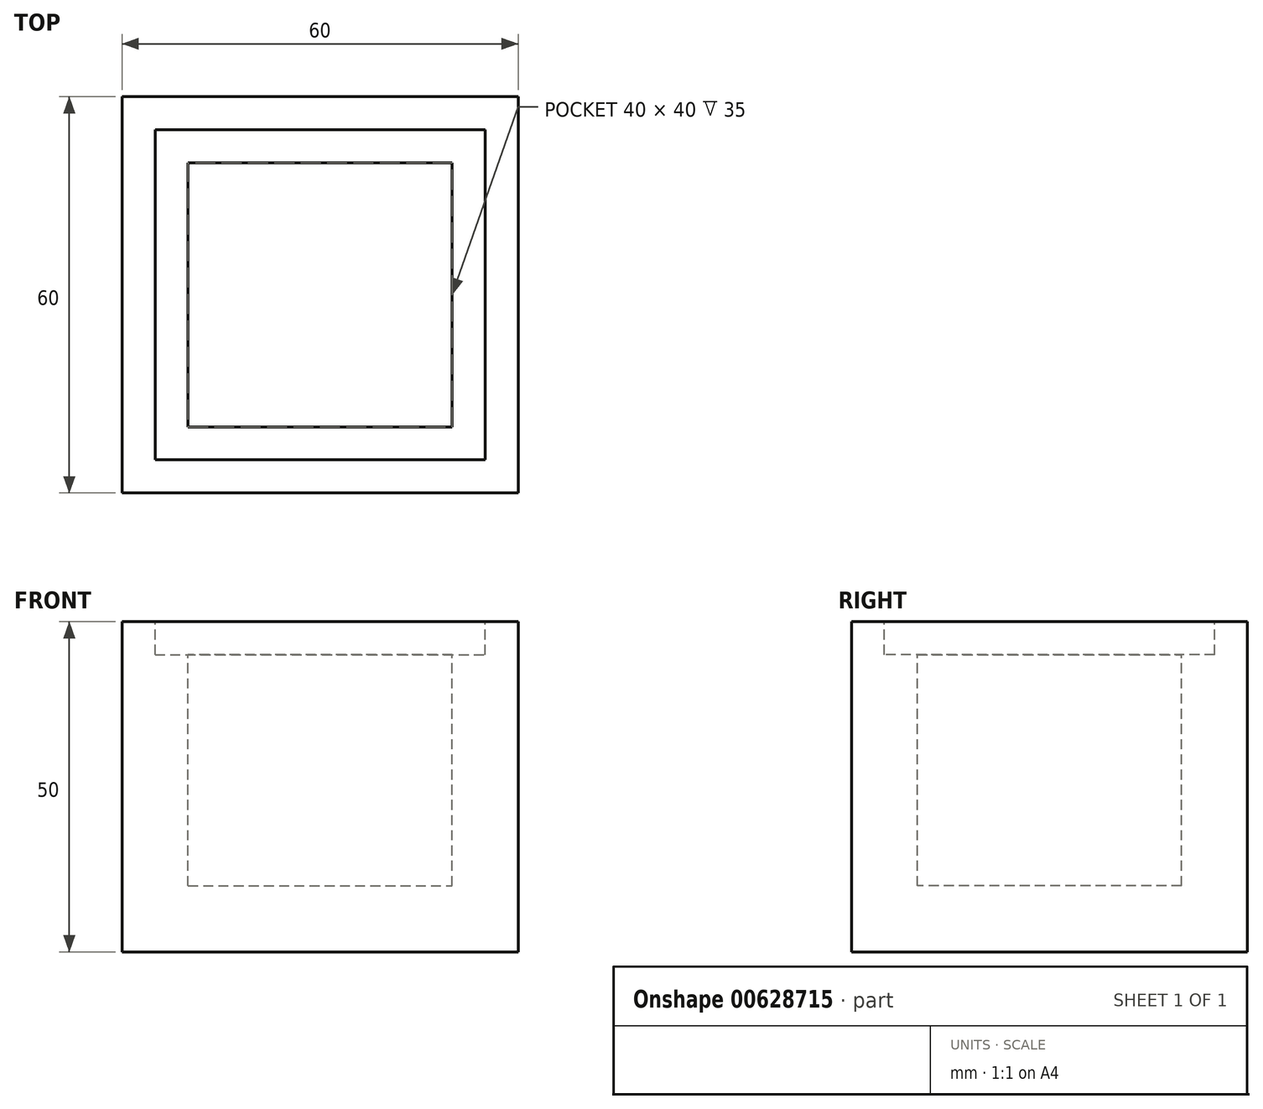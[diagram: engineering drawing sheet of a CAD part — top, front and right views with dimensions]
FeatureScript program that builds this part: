
annotation { "Feature Type Name" : "Feature", "Feature Type Description" : "" }
export const myFeature = defineFeature(function(context is Context, id is Id, definition is map)
    precondition{}
    {
        {
            var Q0;
            Q0=qCreatedBy(makeId("Top.planeOp"),FACE);
            var sketch = newSketch(context, id + "F0", { "sketchPlane" : qUnion([Q0])});
            skLineSegment(sketch, "E0.bottom", {"start": v(0, 0) * mm, "end": v(60, 0) * mm});
            skLineSegment(sketch, "E0.top", {"start": v(0, 60) * mm, "end": v(60, 60) * mm});
            skLineSegment(sketch, "E0.left", {"start": v(0, 0) * mm, "end": v(0, 60) * mm});
            skLineSegment(sketch, "E0.right", {"start": v(60, 0) * mm, "end": v(60, 60) * mm});
            skSolve(sketch);
        }
        {
            var Q0;
            Q0=makeQuery(id+"F0.imprint","IMPRINT",FACE,{"disambiguationData":[TD([[makeQuery(id+"F0.imprint","IMPRINT",EDGE,{"derivedFrom":sQuery(id+"F0.wireOp",EDGE,"E0.bottom")}),1.0]])]});
            var Q1;
            Q1=makeQuery(id+"F0.imprint","IMPRINT",FACE,{"disambiguationData":[TD([[makeQuery(id+"F0.imprint","IMPRINT",EDGE,{"derivedFrom":sQuery(id+"F0.wireOp",EDGE,"qSj7taob-KS4j-ebWW-z35r-J0vfTjwww2YD.bottom")}),-1.0]])]});
            var Q2;
            Q2=makeQuery(id+"F0.imprint","IMPRINT",FACE,{"disambiguationData":[TD([[makeQuery(id+"F0.imprint","IMPRINT",EDGE,{"derivedFrom":sQuery(id+"F0.wireOp",EDGE,"qSj7taob-KS4j-ebWW-z35r-J0vfTjwww2YD.bottom")}),1.0]])]});
            extrude(context, id + "F1", {"entities" : qUnion([Q0, Q1, Q2]), "oppositeDirection" : true, "depth" : 50 * mm, "offsetDistance" : 25 * mm});
        }
        {
            var Q0;
            Q0=qCreatedBy(makeId("Top.planeOp"),FACE);
            var sketch = newSketch(context, id + "F2", { "sketchPlane" : qUnion([Q0])});
            skLineSegment(sketch, "E1.bottom", {"start": v(10, 50) * mm, "end": v(50, 50) * mm});
            skLineSegment(sketch, "E1.top", {"start": v(10, 10) * mm, "end": v(50, 10) * mm});
            skLineSegment(sketch, "E1.left", {"start": v(10, 50) * mm, "end": v(10, 10) * mm});
            skLineSegment(sketch, "E1.right", {"start": v(50, 50) * mm, "end": v(50, 10) * mm});
            skSolve(sketch);
        }
        {
            var Q0;
            Q0 = qSketchRegion(id + "F2", true);
            extrude(context, id + "F3", {"entities" : qUnion([Q0]), "operationType" : NewBodyOperationType.REMOVE, "oppositeDirection" : true, "depth" : 40 * mm, "offsetDistance" : 25 * mm});
        }
        {
            var Q0;
            Q0=qCreatedBy(makeId("Top.planeOp"),FACE);
            var sketch = newSketch(context, id + "F4", { "sketchPlane" : qUnion([Q0])});
            skLineSegment(sketch, "E2.bottom", {"start": v(5, 55) * mm, "end": v(55, 55) * mm});
            skLineSegment(sketch, "E2.top", {"start": v(5, 5) * mm, "end": v(55, 5) * mm});
            skLineSegment(sketch, "E2.left", {"start": v(5, 55) * mm, "end": v(5, 5) * mm});
            skLineSegment(sketch, "E2.right", {"start": v(55, 55) * mm, "end": v(55, 5) * mm});
            skSolve(sketch);
        }
        {
            var Q0;
            Q0 = qSketchRegion(id + "F4", true);
            extrude(context, id + "F5", {"entities" : qUnion([Q0]), "operationType" : NewBodyOperationType.REMOVE, "oppositeDirection" : true, "depth" : 5 * mm, "offsetDistance" : 25 * mm});
        }
    });
